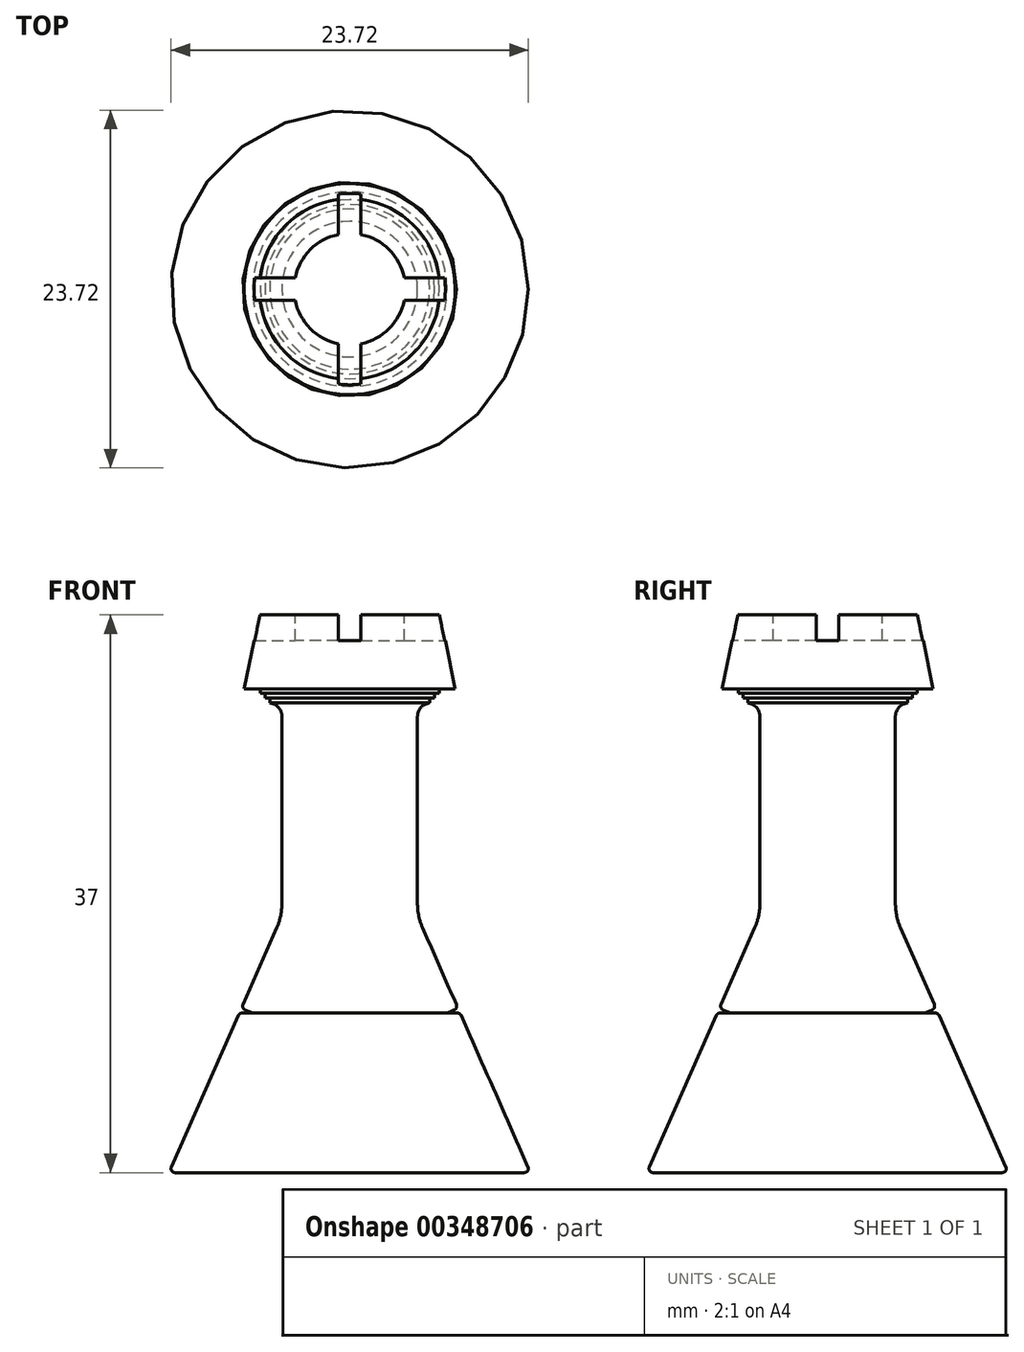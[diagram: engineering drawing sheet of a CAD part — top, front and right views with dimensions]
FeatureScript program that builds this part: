
annotation { "Feature Type Name" : "Feature", "Feature Type Description" : "" }
export const myFeature = defineFeature(function(context is Context, id is Id, definition is map)
    precondition{}
    {
        {
            var Q0;
            Q0=qCreatedBy(makeId("Front.planeOp"),FACE);
            var sketch = newSketch(context, id + "F0", { "sketchPlane" : qUnion([Q0])});
            skLineSegment(sketch, "E0", {"start": v(0, 0) * mm, "end": v(11.59, 0) * mm});
            skLineSegment(sketch, "E1", {"start": v(11.83, 0.38) * mm, "end": v(7.4, 10.42) * mm});
            skLineSegment(sketch, "E2", {"start": v(4.5, 17.84) * mm, "end": v(4.5, 30.26) * mm});
            skLineSegment(sketch, "E3", {"start": v(7, 32.1) * mm, "end": v(6, 37) * mm});
            skLineSegment(sketch, "E4", {"start": v(6, 37) * mm, "end": v(3.7, 37) * mm});
            skLineSegment(sketch, "E5", {"start": v(0, 35.3) * mm, "end": v(0, 0) * mm});
            skLineSegment(sketch, "E6", {"start": v(5.22, 31.14) * mm, "end": v(5.3, 31.16) * mm});
            skLineSegment(sketch, "E7", {"start": v(5.3, 31.16) * mm, "end": v(5.3, 31.47) * mm});
            skLineSegment(sketch, "E8", {"start": v(5.3, 31.47) * mm, "end": v(5.62, 31.47) * mm});
            skLineSegment(sketch, "E9", {"start": v(5.62, 31.47) * mm, "end": v(5.62, 31.79) * mm});
            skLineSegment(sketch, "E10", {"start": v(5.62, 31.79) * mm, "end": v(5.93, 31.79) * mm});
            skLineSegment(sketch, "E11", {"start": v(5.93, 31.79) * mm, "end": v(5.93, 32.1) * mm});
            skLineSegment(sketch, "E12", {"start": v(5.93, 32.1) * mm, "end": v(7, 32.1) * mm});
            skPoint(sketch, "E13.visualSharp", {"position": v(4.5, 31) * mm});
            skArc(sketch, "E13.filletArc", {"start": v(5.22, 31.14) * mm, "mid": v(4.7, 30.83) * mm, "end": v(4.5, 30.26) * mm});
            skLineSegment(sketch, "E14", {"start": v(6.94, 10.8) * mm, "end": v(6.45, 10.58) * mm});
            skLineSegment(sketch, "E15", {"start": v(6.45, 10.58) * mm, "end": v(7.16, 10.58) * mm});
            skLineSegment(sketch, "E16.trimOffspring", {"start": v(7.08, 11.15) * mm, "end": v(4.84, 16.23) * mm});
            skPoint(sketch, "E17.visualSharp", {"position": v(4.5, 17) * mm});
            skArc(sketch, "E17.filletArc", {"start": v(4.5, 17.84) * mm, "mid": v(4.59, 17.02) * mm, "end": v(4.84, 16.23) * mm});
            skPoint(sketch, "E18.visualSharp", {"position": v(7.19, 10.9) * mm});
            skArc(sketch, "E18.filletArc", {"start": v(6.94, 10.8) * mm, "mid": v(7.08, 10.95) * mm, "end": v(7.08, 11.15) * mm});
            skPoint(sketch, "E19.visualSharp", {"position": v(7.33, 10.58) * mm});
            skArc(sketch, "E19.filletArc", {"start": v(7.4, 10.42) * mm, "mid": v(7.3, 10.54) * mm, "end": v(7.16, 10.58) * mm});
            skPoint(sketch, "E20.visualSharp", {"position": v(12, 0) * mm});
            skArc(sketch, "E20.filletArc", {"start": v(11.59, 0) * mm, "mid": v(11.81, 0.12) * mm, "end": v(11.83, 0.38) * mm});
            skLineSegment(sketch, "E21", {"start": v(0, 46.66) * mm, "end": v(0, 37) * mm, "construction": true});
            skLineSegment(sketch, "E22", {"start": v(3.7, 37) * mm, "end": v(3.7, 35.3) * mm});
            skLineSegment(sketch, "E23", {"start": v(3.7, 35.3) * mm, "end": v(0, 35.3) * mm});
            skLineSegment(sketch, "E24.trimOffspring", {"start": v(0, 35.3) * mm, "end": v(0, -10.07) * mm, "construction": true});
            skSolve(sketch);
        }
        {
            var Q0;
            Q0 = qSketchRegion(id + "F0", true);
            var Q1;
            Q1=sQuery(id+"F0.wireOp",EDGE,"E21");
            revolve(context, id + "F1", {"entities" : qUnion([Q0]), "axis" : qUnion([Q1]), "revolveType" : RevolveType.FULL});
        }
        {
            var Q0;
            Q0=makeQuery(id+"F1.opRevolve","SWEPT_FACE",FACE,{"disambiguationData":[OSD([sQuery(id+"F0.wireOp",EDGE,"E23")])]});
            var sketch = newSketch(context, id + "F2", { "sketchPlane" : qUnion([Q0])});
            skLineSegment(sketch, "E25.bottom", {"start": v(-12.71, 0.75) * mm, "end": v(15.7, 0.75) * mm});
            skLineSegment(sketch, "E25.top", {"start": v(-12.71, -0.75) * mm, "end": v(15.7, -0.75) * mm});
            skLineSegment(sketch, "E25.left", {"start": v(-12.71, 0.75) * mm, "end": v(-12.71, -0.75) * mm});
            skLineSegment(sketch, "E25.right", {"start": v(15.7, 0.75) * mm, "end": v(15.7, -0.75) * mm});
            skLineSegment(sketch, "E26", {"start": v(0, 0.75) * mm, "end": v(0, 0) * mm});
            skLineSegment(sketch, "E27", {"start": v(0, 0) * mm, "end": v(0, -0.75) * mm});
            skLineSegment(sketch, "E28.bottom", {"start": v(-0.75, 10.01) * mm, "end": v(0.75, 10.01) * mm});
            skLineSegment(sketch, "E28.top", {"start": v(-0.75, -9.99) * mm, "end": v(0.75, -9.99) * mm});
            skLineSegment(sketch, "E28.left", {"start": v(-0.75, 10.01) * mm, "end": v(-0.75, -9.99) * mm});
            skLineSegment(sketch, "E28.right", {"start": v(0.75, 10.01) * mm, "end": v(0.75, -9.99) * mm});
            skLineSegment(sketch, "E29", {"start": v(0, 0) * mm, "end": v(-0.75, 0) * mm});
            skLineSegment(sketch, "E30", {"start": v(0, 0) * mm, "end": v(0.75, 0) * mm});
            skSolve(sketch);
        }
        {
            var Q0;
            Q0 = qSketchRegion(id + "F2", true);
            extrude(context, id + "F3", {"entities" : qUnion([Q0]), "operationType" : NewBodyOperationType.REMOVE, "depth" : 25 * mm});
        }
    });
